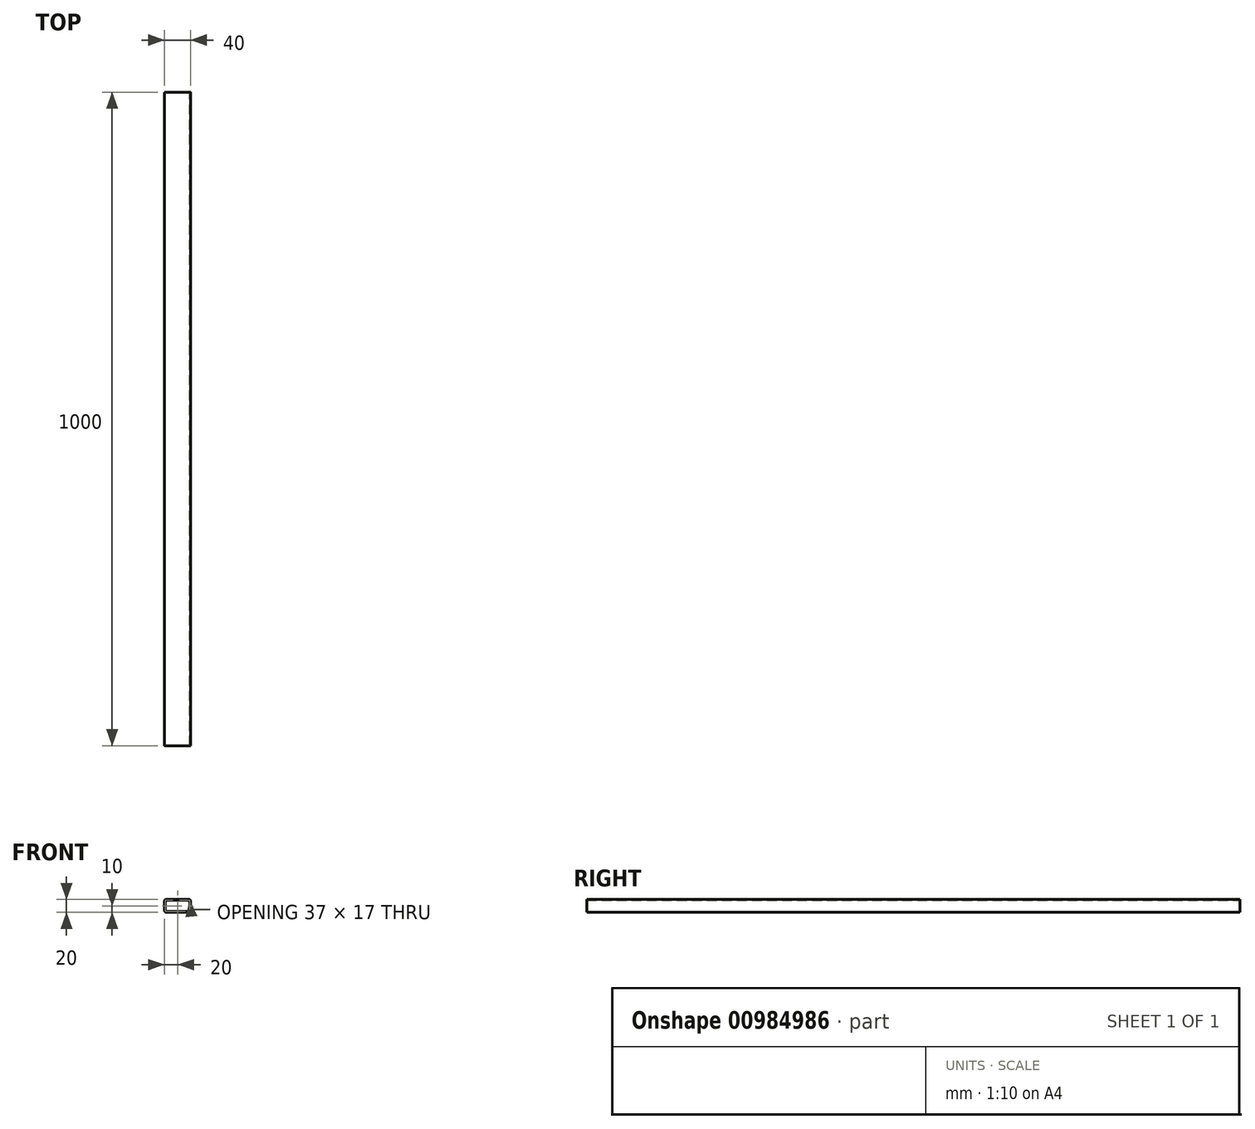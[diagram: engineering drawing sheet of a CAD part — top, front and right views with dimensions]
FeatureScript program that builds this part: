
annotation { "Feature Type Name" : "Feature", "Feature Type Description" : "" }
export const myFeature = defineFeature(function(context is Context, id is Id, definition is map)
    precondition{}
    {
        {
            var Q0;
            Q0=qCreatedBy(makeId("Front.planeOp"),FACE);
            var sketch = newSketch(context, id + "F0", { "sketchPlane" : qUnion([Q0])});
            skLineSegment(sketch, "E0.bottom", {"start": v(-17, 10) * mm, "end": v(17, 10) * mm});
            skLineSegment(sketch, "E0.top", {"start": v(-17, -10) * mm, "end": v(17, -10) * mm});
            skLineSegment(sketch, "E0.left", {"start": v(-20, 7) * mm, "end": v(-20, -7) * mm});
            skLineSegment(sketch, "E0.right", {"start": v(20, 7) * mm, "end": v(20, -7) * mm});
            skLineSegment(sketch, "E1.0", {"start": v(18.5, 5.5) * mm, "end": v(18.5, -5.5) * mm});
            skLineSegment(sketch, "E1.1", {"start": v(-15.5, 8.5) * mm, "end": v(15.5, 8.5) * mm});
            skLineSegment(sketch, "E1.2", {"start": v(-18.5, 5.5) * mm, "end": v(-18.5, -5.5) * mm});
            skLineSegment(sketch, "E1.3", {"start": v(-15.5, -8.5) * mm, "end": v(15.5, -8.5) * mm});
            skPoint(sketch, "E2.visualSharp", {"position": v(20, 10) * mm});
            skArc(sketch, "E2.filletArc", {"start": v(20, 7) * mm, "mid": v(19.12, 9.12) * mm, "end": v(17, 10) * mm});
            skPoint(sketch, "E3.visualSharp", {"position": v(18.5, 8.5) * mm});
            skArc(sketch, "E3.filletArc", {"start": v(18.5, 5.5) * mm, "mid": v(17.62, 7.62) * mm, "end": v(15.5, 8.5) * mm});
            skPoint(sketch, "E4.visualSharp", {"position": v(-18.5, -8.5) * mm});
            skArc(sketch, "E4.filletArc", {"start": v(-18.5, -5.5) * mm, "mid": v(-17.62, -7.62) * mm, "end": v(-15.5, -8.5) * mm});
            skPoint(sketch, "E5.visualSharp", {"position": v(-20, -10) * mm});
            skArc(sketch, "E5.filletArc", {"start": v(-20, -7) * mm, "mid": v(-19.12, -9.12) * mm, "end": v(-17, -10) * mm});
            skPoint(sketch, "E6.visualSharp", {"position": v(-18.5, 8.5) * mm});
            skArc(sketch, "E6.filletArc", {"start": v(-15.5, 8.5) * mm, "mid": v(-17.62, 7.62) * mm, "end": v(-18.5, 5.5) * mm});
            skPoint(sketch, "E7.visualSharp", {"position": v(-20, 10) * mm});
            skArc(sketch, "E7.filletArc", {"start": v(-17, 10) * mm, "mid": v(-19.12, 9.12) * mm, "end": v(-20, 7) * mm});
            skPoint(sketch, "E8.visualSharp", {"position": v(18.5, -8.5) * mm});
            skArc(sketch, "E8.filletArc", {"start": v(15.5, -8.5) * mm, "mid": v(17.62, -7.62) * mm, "end": v(18.5, -5.5) * mm});
            skPoint(sketch, "E9.visualSharp", {"position": v(20, -10) * mm});
            skArc(sketch, "E9.filletArc", {"start": v(17, -10) * mm, "mid": v(19.12, -9.12) * mm, "end": v(20, -7) * mm});
            skSolve(sketch);
        }
        {
            var Q0;
            Q0=makeQuery(id+"F0.imprint","IMPRINT",FACE,{"disambiguationData":[TD([[makeQuery(id+"F0.imprint","IMPRINT",EDGE,{"derivedFrom":sQuery(id+"F0.wireOp",EDGE,"E0.bottom")}),-1.0]])]});
            extrude(context, id + "F1", {"entities" : qUnion([Q0]), "depth" : 1000 * mm, "offsetDistance" : 25.4 * mm});
        }
    });
